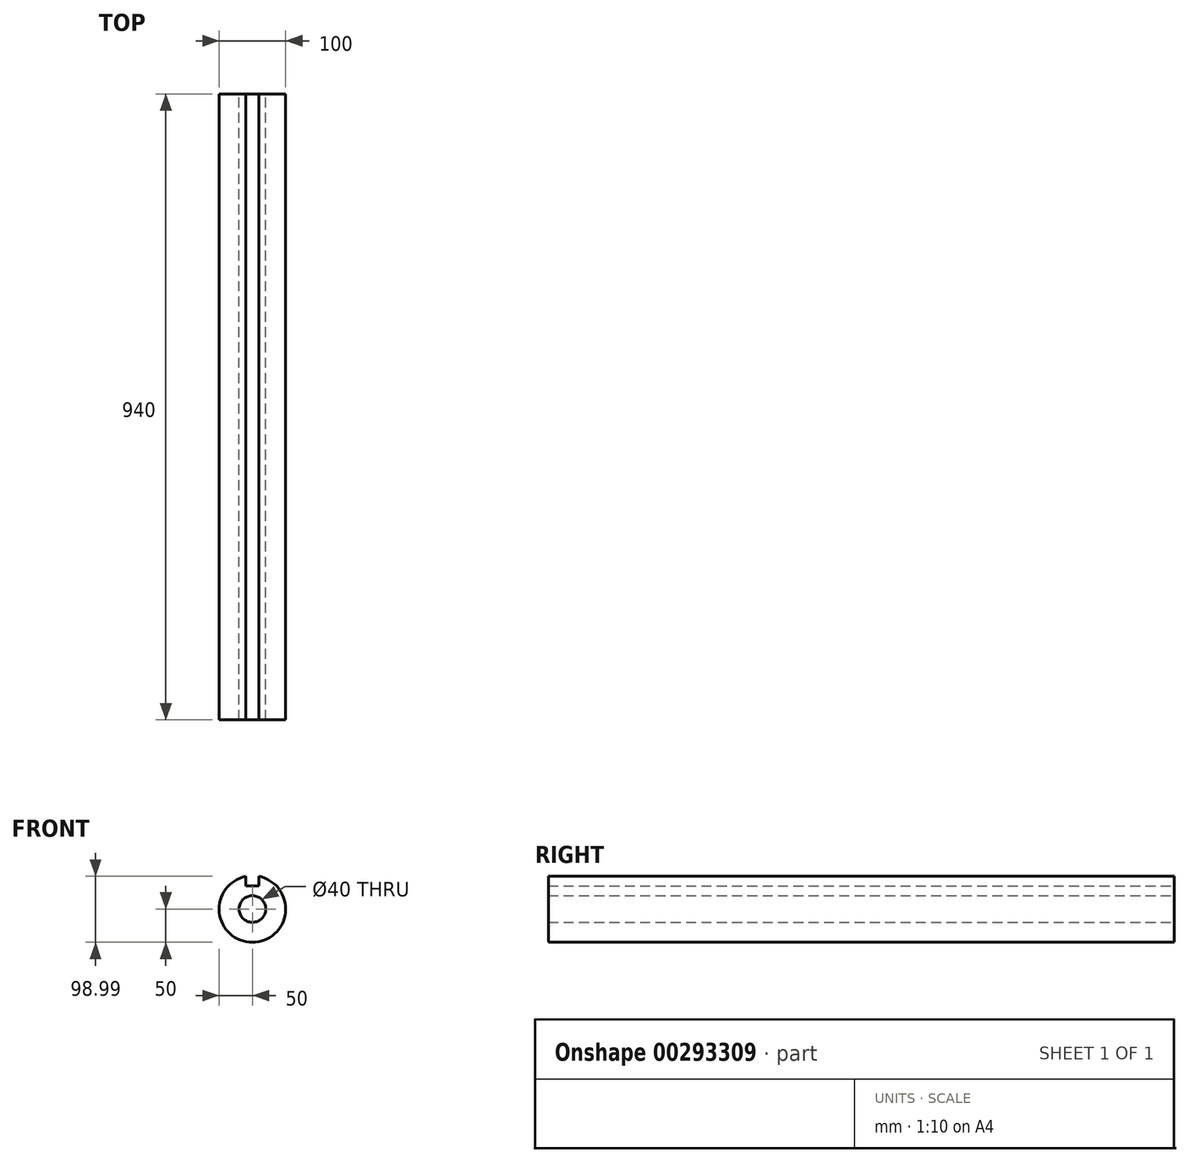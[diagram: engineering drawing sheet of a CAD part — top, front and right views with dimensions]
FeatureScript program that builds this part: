
annotation { "Feature Type Name" : "Feature", "Feature Type Description" : "" }
export const myFeature = defineFeature(function(context is Context, id is Id, definition is map)
    precondition{}
    {
        {
            var Q0;
            Q0=qCreatedBy(makeId("Front.planeOp"),FACE);
            var sketch = newSketch(context, id + "F0", { "sketchPlane" : qUnion([Q0])});
            skCircle(sketch, "E0", {"center": v(0, 0) * mm, "radius": 237.5 * mm, "construction": true});
            skArc(sketch, "E1.1.0", {"start": v(-230.76, 110.13) * mm, "mid": v(-122.6, 70.78) * mm, "end": v(-210.76, 144.77) * mm});
            skLineSegment(sketch, "E1.1.1", {"start": v(-163.2, 117.32) * mm, "end": v(-210.76, 144.77) * mm});
            skLineSegment(sketch, "E1.1.2", {"start": v(-173.2, 100) * mm, "end": v(-220.76, 127.45) * mm, "construction": true});
            skLineSegment(sketch, "E1.1.3", {"start": v(-183.2, 82.68) * mm, "end": v(-230.76, 110.13) * mm});
            skLineSegment(sketch, "E1.1.4", {"start": v(-183.2, 82.68) * mm, "end": v(-163.2, 117.32) * mm});
            skArc(sketch, "E1.2.0", {"start": v(-210.76, -144.77) * mm, "mid": v(-122.6, -70.78) * mm, "end": v(-230.76, -110.13) * mm});
            skLineSegment(sketch, "E1.2.1", {"start": v(-183.2, -82.68) * mm, "end": v(-230.76, -110.13) * mm});
            skLineSegment(sketch, "E1.2.2", {"start": v(-173.2, -100) * mm, "end": v(-220.76, -127.45) * mm, "construction": true});
            skLineSegment(sketch, "E1.2.3", {"start": v(-163.2, -117.32) * mm, "end": v(-210.76, -144.77) * mm});
            skLineSegment(sketch, "E1.2.4", {"start": v(-163.2, -117.32) * mm, "end": v(-183.2, -82.68) * mm});
            skArc(sketch, "E1.3.0", {"start": v(20, -254.9) * mm, "mid": v(0, -141.56) * mm, "end": v(-20, -254.9) * mm});
            skLineSegment(sketch, "E1.3.1", {"start": v(-20, -200) * mm, "end": v(-20, -254.9) * mm});
            skLineSegment(sketch, "E1.3.2", {"start": v(0, -200) * mm, "end": v(0, -254.9) * mm, "construction": true});
            skLineSegment(sketch, "E1.3.3", {"start": v(20, -200) * mm, "end": v(20, -254.9) * mm});
            skLineSegment(sketch, "E1.3.4", {"start": v(20, -200) * mm, "end": v(-20, -200) * mm});
            skArc(sketch, "E1.4.0", {"start": v(230.76, -110.13) * mm, "mid": v(122.6, -70.78) * mm, "end": v(210.76, -144.77) * mm});
            skLineSegment(sketch, "E1.4.1", {"start": v(163.2, -117.32) * mm, "end": v(210.76, -144.77) * mm});
            skLineSegment(sketch, "E1.4.2", {"start": v(173.2, -100) * mm, "end": v(220.76, -127.45) * mm, "construction": true});
            skLineSegment(sketch, "E1.4.3", {"start": v(183.2, -82.68) * mm, "end": v(230.76, -110.13) * mm});
            skLineSegment(sketch, "E1.4.4", {"start": v(183.2, -82.68) * mm, "end": v(163.2, -117.32) * mm});
            skArc(sketch, "E1.5.0", {"start": v(210.76, 144.77) * mm, "mid": v(122.6, 70.78) * mm, "end": v(230.76, 110.13) * mm});
            skLineSegment(sketch, "E1.5.1", {"start": v(183.2, 82.68) * mm, "end": v(230.76, 110.13) * mm});
            skLineSegment(sketch, "E1.5.2", {"start": v(173.2, 100) * mm, "end": v(220.76, 127.45) * mm, "construction": true});
            skLineSegment(sketch, "E1.5.3", {"start": v(163.2, 117.32) * mm, "end": v(210.76, 144.77) * mm});
            skLineSegment(sketch, "E1.5.4", {"start": v(163.2, 117.32) * mm, "end": v(183.2, 82.68) * mm});
            skArc(sketch, "E2", {"start": v(-10, 248.99) * mm, "mid": v(0, 150) * mm, "end": v(10, 248.99) * mm});
            skCircle(sketch, "E3", {"center": v(0, 200) * mm, "radius": 20 * mm});
            skLineSegment(sketch, "E4", {"start": v(0, 200) * mm, "end": v(0, 0) * mm, "construction": true});
            skLineSegment(sketch, "E5.top", {"start": v(-10, 234.67) * mm, "end": v(10, 234.67) * mm});
            skLineSegment(sketch, "E5.left", {"start": v(-10, 234.67) * mm, "end": v(-10, 248.99) * mm});
            skLineSegment(sketch, "E5.right", {"start": v(10, 234.67) * mm, "end": v(10, 248.99) * mm});
            skLineSegment(sketch, "E6", {"start": v(0, 234.67) * mm, "end": v(0, 248.99) * mm, "construction": true});
            skSolve(sketch);
        }
        {
            var Q0;
            Q0=makeQuery(id+"F0.imprint","IMPRINT",FACE,{"disambiguationData":[TD([[makeQuery(id+"F0.imprint","IMPRINT",EDGE,{"derivedFrom":sQuery(id+"F0.wireOp",EDGE,"E2")}),1.0]])]});
            extrude(context, id + "F1", {"entities" : qUnion([Q0]), "depth" : 470 * mm, "hasSecondDirection" : true, "secondDirectionOppositeDirection" : true, "secondDirectionDepth" : 470 * mm});
        }
    });
